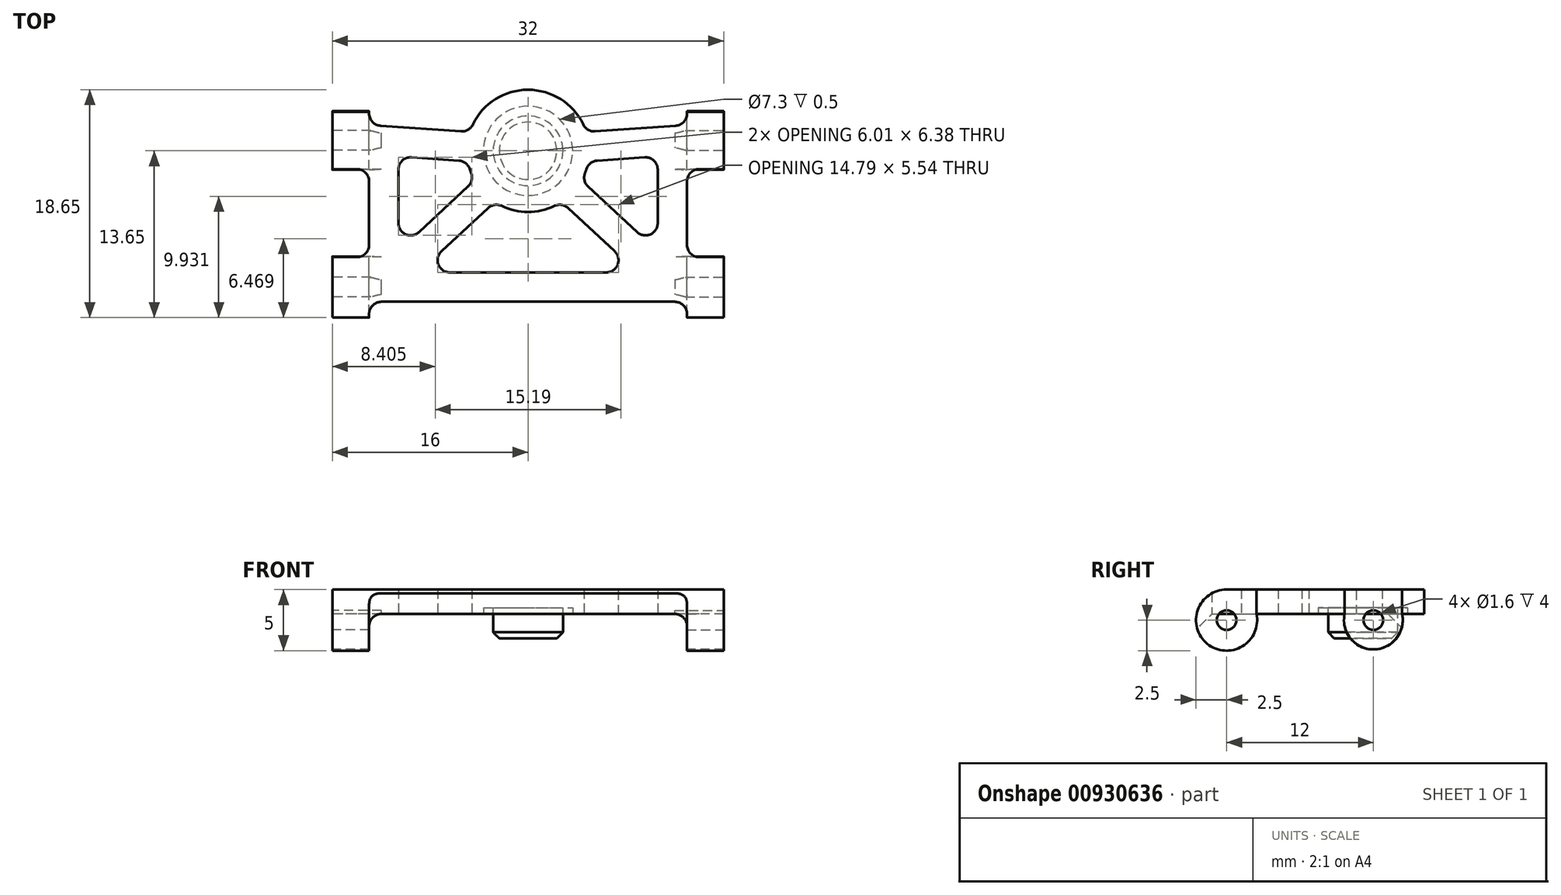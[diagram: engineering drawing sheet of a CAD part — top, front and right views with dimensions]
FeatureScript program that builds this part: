
annotation { "Feature Type Name" : "Feature", "Feature Type Description" : "" }
export const myFeature = defineFeature(function(context is Context, id is Id, definition is map)
    precondition{}
    {
        {
            var Q0;
            Q0=qCreatedBy(makeId("Right.planeOp"),FACE);
            var sketch = newSketch(context, id + "F0", { "sketchPlane" : qUnion([Q0])});
            skArc(sketch, "E0", {"start": v(0, 2.5) * mm, "mid": v(-1.58, -1.94) * mm, "end": v(2.45, 0.5) * mm});
            skArc(sketch, "E1", {"start": v(9.65, 0.5) * mm, "mid": v(12, -2.4) * mm, "end": v(14.35, 0.5) * mm});
            skLineSegment(sketch, "E2", {"start": v(2.45, 0.5) * mm, "end": v(9.65, 0.5) * mm});
            skLineSegment(sketch, "E3", {"start": v(16.35, 2.5) * mm, "end": v(16.35, 0.5) * mm});
            skLineSegment(sketch, "E4", {"start": v(16.35, 0.5) * mm, "end": v(14.35, 0.5) * mm});
            skLineSegment(sketch, "E5", {"start": v(16.35, 2.5) * mm, "end": v(0, 2.5) * mm});
            skSolve(sketch);
        }
        {
            var Q0;
            Q0=qSketchRegion(id+"F0",true);
            extrude(context, id + "F1", {"entities" : qUnion([Q0]), "depth" : 32 * mm, "offsetDistance" : 25 * mm});
        }
        {
            var Q0;
            Q0=makeQuery(id+"F1.opExtrude","SWEPT_FACE",FACE,{"disambiguationData":[OSD([sQuery(id+"F0.wireOp",EDGE,"E3")])]});
            var sketch = newSketch(context, id + "F2", { "sketchPlane" : qUnion([Q0])});
            skLineSegment(sketch, "E6.bottom", {"start": v(-29, 0.5) * mm, "end": v(-3, 0.5) * mm});
            skLineSegment(sketch, "E6.top", {"start": v(-29, -2.5) * mm, "end": v(-3, -2.5) * mm});
            skLineSegment(sketch, "E6.left", {"start": v(-29, 0.5) * mm, "end": v(-29, -2.5) * mm});
            skLineSegment(sketch, "E6.right", {"start": v(-3, 0.5) * mm, "end": v(-3, -2.5) * mm});
            skSolve(sketch);
        }
        {
            var Q0;
            Q0=qSketchRegion(id+"F2",true);
            extrude(context, id + "F3", {"entities" : qUnion([Q0]), "operationType" : NewBodyOperationType.REMOVE, "endBound" : BoundingType.THROUGH_ALL, "oppositeDirection" : true, "depth" : 25 * mm, "offsetDistance" : 25 * mm});
        }
        {
            var Q0;
            Q0=makeQuery(id+"F1.opExtrude","CAP_FACE",FACE,{"disambiguationData":[OSD([sQuery(id+"F0.wireOp",EDGE,"E0"),sQuery(id+"F0.wireOp",EDGE,"E1"),sQuery(id+"F0.wireOp",EDGE,"E2"),sQuery(id+"F0.wireOp",EDGE,"E3"),sQuery(id+"F0.wireOp",EDGE,"E4"),sQuery(id+"F0.wireOp",EDGE,"E5")])],"isStart":false});
            var sketch = newSketch(context, id + "F4", { "sketchPlane" : qUnion([Q0])});
            skCircle(sketch, "E7", {"center": v(0, 0) * mm, "radius": 0.8 * mm});
            skCircle(sketch, "E8", {"center": v(12, 0) * mm, "radius": 0.8 * mm});
            skSolve(sketch);
        }
        {
            var Q0;
            Q0=qSketchRegion(id+"F4",true);
            extrude(context, id + "F5", {"entities" : qUnion([Q0]), "operationType" : NewBodyOperationType.REMOVE, "oppositeDirection" : true, "depth" : 4 * mm, "offsetDistance" : 25 * mm});
        }
        {
            var Q0;
            Q0=makeQuery(id+"F1.opExtrude","CAP_FACE",FACE,{"disambiguationData":[OSD([sQuery(id+"F0.wireOp",EDGE,"E0"),sQuery(id+"F0.wireOp",EDGE,"E1"),sQuery(id+"F0.wireOp",EDGE,"E2"),sQuery(id+"F0.wireOp",EDGE,"E3"),sQuery(id+"F0.wireOp",EDGE,"E4"),sQuery(id+"F0.wireOp",EDGE,"E5")])],"isStart":true});
            var sketch = newSketch(context, id + "F6", { "sketchPlane" : qUnion([Q0])});
            skCircle(sketch, "E9", {"center": v(0, 0) * mm, "radius": 0.8 * mm});
            skCircle(sketch, "E10", {"center": v(-12, 0) * mm, "radius": 0.8 * mm});
            skSolve(sketch);
        }
        {
            var Q0;
            Q0=qSketchRegion(id+"F6",true);
            extrude(context, id + "F7", {"entities" : qUnion([Q0]), "operationType" : NewBodyOperationType.REMOVE, "oppositeDirection" : true, "depth" : 4 * mm, "offsetDistance" : 25 * mm});
        }
        {
            var Q0;
            Q0=makeQuery(id+"F3.boolean.opBoolean","MERGE",FACE,{"derivedFrom":[makeQuery(id+"F1.opExtrude","SWEPT_FACE",FACE,{"disambiguationData":[OSD([sQuery(id+"F0.wireOp",EDGE,"E2")])]}),makeQuery(id+"F1.opExtrude","SWEPT_FACE",FACE,{"disambiguationData":[OSD([sQuery(id+"F0.wireOp",EDGE,"E4")])]}),makeQuery(id+"F3.opExtrude","SWEPT_FACE",FACE,{"disambiguationData":[OSD([sQuery(id+"F2.wireOp",EDGE,"E6.bottom")])]})]});
            var sketch = newSketch(context, id + "F8", { "sketchPlane" : qUnion([Q0])});
            skLineSegment(sketch, "E11", {"start": v(16, 2.45) * mm, "end": v(16, -16.35) * mm, "construction": true});
            skCircle(sketch, "E12", {"center": v(16, -11.15) * mm, "radius": 2.85 * mm});
            skSolve(sketch);
        }
        {
            var Q0;
            Q0=qSketchRegion(id+"F8",true);
            extrude(context, id + "F9", {"entities" : qUnion([Q0]), "operationType" : NewBodyOperationType.ADD, "depth" : 2 * mm, "offsetDistance" : 25 * mm});
        }
        {
            var Q0;
            Q0=makeQuery(id+"F3.boolean.opBoolean","MERGE",FACE,{"derivedFrom":[makeQuery(id+"F1.opExtrude","SWEPT_FACE",FACE,{"disambiguationData":[OSD([sQuery(id+"F0.wireOp",EDGE,"E2")])]}),makeQuery(id+"F1.opExtrude","SWEPT_FACE",FACE,{"disambiguationData":[OSD([sQuery(id+"F0.wireOp",EDGE,"E4")])]}),makeQuery(id+"F3.opExtrude","SWEPT_FACE",FACE,{"disambiguationData":[OSD([sQuery(id+"F2.wireOp",EDGE,"E6.bottom")])]})]});
            var sketch = newSketch(context, id + "F10", { "sketchPlane" : qUnion([Q0])});
            skArc(sketch, "E13", {"start": v(18.74, -6.97) * mm, "mid": v(16, -6.15) * mm, "end": v(13.26, -6.97) * mm});
            skLineSegment(sketch, "E14.bottom", {"start": v(0, -2.45) * mm, "end": v(3, -2.45) * mm});
            skLineSegment(sketch, "E14.top", {"start": v(0, -9.65) * mm, "end": v(3, -9.65) * mm});
            skLineSegment(sketch, "E14.left", {"start": v(0, -2.45) * mm, "end": v(0, -9.65) * mm});
            skLineSegment(sketch, "E14.right", {"start": v(3, -2.45) * mm, "end": v(3, -9.65) * mm});
            skLineSegment(sketch, "E15.bottom", {"start": v(29, -2.45) * mm, "end": v(32, -2.45) * mm});
            skLineSegment(sketch, "E15.top", {"start": v(29, -9.65) * mm, "end": v(32, -9.65) * mm});
            skLineSegment(sketch, "E15.left", {"start": v(29, -2.45) * mm, "end": v(29, -9.65) * mm});
            skLineSegment(sketch, "E15.right", {"start": v(32, -2.45) * mm, "end": v(32, -9.65) * mm});
            skLineSegment(sketch, "E16.bottom", {"start": v(0, -14.35) * mm, "end": v(3, -14.35) * mm});
            skLineSegment(sketch, "E16.left", {"start": v(0, -14.35) * mm, "end": v(0, -16.35) * mm});
            skLineSegment(sketch, "E17.bottom", {"start": v(29, -14.35) * mm, "end": v(32, -14.35) * mm});
            skLineSegment(sketch, "E17.right", {"start": v(32, -14.35) * mm, "end": v(32, -16.35) * mm});
            skLineSegment(sketch, "E18", {"start": v(3, 1.2) * mm, "end": v(29, 1.2) * mm});
            skLineSegment(sketch, "E19", {"start": v(4, 0) * mm, "end": v(28, 0) * mm, "construction": true});
            skLineSegment(sketch, "E20", {"start": v(4, -12) * mm, "end": v(16, -11.15) * mm, "construction": true});
            skLineSegment(sketch, "E21", {"start": v(28, -12) * mm, "end": v(16, -11.15) * mm, "construction": true});
            skLineSegment(sketch, "E22", {"start": v(4, 0) * mm, "end": v(16, -11.15) * mm, "construction": true});
            skLineSegment(sketch, "E23", {"start": v(16, -11.15) * mm, "end": v(28, 0) * mm, "construction": true});
            skLineSegment(sketch, "E24", {"start": v(5.4, -10.7) * mm, "end": v(11.07, -10.3) * mm});
            skLineSegment(sketch, "E25", {"start": v(3, -13.27) * mm, "end": v(11.24, -12.69) * mm});
            skLineSegment(sketch, "E26", {"start": v(26.6, -10.7) * mm, "end": v(20.93, -10.3) * mm});
            skLineSegment(sketch, "E27", {"start": v(29, -13.27) * mm, "end": v(20.76, -12.69) * mm});
            skLineSegment(sketch, "E28", {"start": v(3, -13.27) * mm, "end": v(3, -14.35) * mm});
            skLineSegment(sketch, "E29", {"start": v(29, -13.27) * mm, "end": v(29, -14.35) * mm});
            skLineSegment(sketch, "E30", {"start": v(0, -16.35) * mm, "end": v(16, -16.35) * mm});
            skLineSegment(sketch, "E31", {"start": v(16, -16.35) * mm, "end": v(32, -16.35) * mm});
            skLineSegment(sketch, "E32", {"start": v(7.05, -1.2) * mm, "end": v(13.26, -6.97) * mm});
            skLineSegment(sketch, "E33", {"start": v(24.95, -1.2) * mm, "end": v(18.74, -6.97) * mm});
            skLineSegment(sketch, "E34", {"start": v(5.4, -2.94) * mm, "end": v(11.63, -8.73) * mm});
            skLineSegment(sketch, "E35", {"start": v(26.6, -2.94) * mm, "end": v(20.37, -8.73) * mm});
            skLineSegment(sketch, "E36", {"start": v(5.4, -2.94) * mm, "end": v(5.4, -10.7) * mm});
            skLineSegment(sketch, "E37", {"start": v(26.6, -2.94) * mm, "end": v(26.6, -10.7) * mm});
            skLineSegment(sketch, "E38.trimOffspring", {"start": v(7.05, -1.2) * mm, "end": v(24.95, -1.2) * mm});
            skLineSegment(sketch, "E39", {"start": v(3, 1.2) * mm, "end": v(3, 2.45) * mm});
            skLineSegment(sketch, "E40", {"start": v(3, 2.45) * mm, "end": v(29, 2.45) * mm});
            skLineSegment(sketch, "E41", {"start": v(29, 2.45) * mm, "end": v(29, 1.2) * mm});
            skArc(sketch, "E42.trimOffspring", {"start": v(11.63, -8.73) * mm, "mid": v(11.28, -9.49) * mm, "end": v(11.07, -10.3) * mm});
            skArc(sketch, "E43.trimOffspring", {"start": v(11.24, -12.69) * mm, "mid": v(16, -16.15) * mm, "end": v(20.76, -12.69) * mm});
            skArc(sketch, "E44.trimOffspring", {"start": v(20.93, -10.3) * mm, "mid": v(20.72, -9.49) * mm, "end": v(20.37, -8.73) * mm});
            skPoint(sketch, "E45", {"position": v(28, 0) * mm});
            skSolve(sketch);
        }
        {
            var Q0;
            Q0=qSketchRegion(id+"F10",true);
            extrude(context, id + "F11", {"entities" : qUnion([Q0]), "operationType" : NewBodyOperationType.REMOVE, "endBound" : BoundingType.UP_TO_NEXT, "oppositeDirection" : true, "depth" : 25 * mm, "offsetDistance" : 25 * mm});
        }
        {
            var Q0;
            Q0=makeQuery(id+"F11.boolean.opBoolean","COPY",EDGE,{"derivedFrom":makeQuery(id+"F11.opExtrude","SWEPT_EDGE",EDGE,{"disambiguationData":[OSD([sQuery(id+"F0.wireOp",EDGE,"E1"),sQuery(id+"F0.wireOp",EDGE,"E3"),sQuery(id+"F0.wireOp",EDGE,"E4"),sQuery(id+"F2.wireOp",EDGE,"E6.bottom"),sQuery(id+"F2.wireOp",EDGE,"E6.left"),sQuery(id+"F10.wireOp",EDGE,"E15.top"),sQuery(id+"F10.wireOp",EDGE,"E15.left")])]})});
            var Q1;
            Q1=makeQuery(id+"F11.boolean.opBoolean","COPY",EDGE,{"derivedFrom":makeQuery(id+"F11.opExtrude","SWEPT_EDGE",EDGE,{"disambiguationData":[OSD([sQuery(id+"F0.wireOp",EDGE,"E0"),sQuery(id+"F0.wireOp",EDGE,"E3"),sQuery(id+"F0.wireOp",EDGE,"E4"),sQuery(id+"F2.wireOp",EDGE,"E6.bottom"),sQuery(id+"F2.wireOp",EDGE,"E6.left"),sQuery(id+"F10.wireOp",EDGE,"E15.bottom"),sQuery(id+"F10.wireOp",EDGE,"E15.left")])]})});
            var Q2;
            Q2=makeQuery(id+"F11.boolean.opBoolean","COPY",EDGE,{"derivedFrom":makeQuery(id+"F11.opExtrude","SWEPT_EDGE",EDGE,{"disambiguationData":[OSD([sQuery(id+"F0.wireOp",EDGE,"E0"),sQuery(id+"F0.wireOp",EDGE,"E3"),sQuery(id+"F0.wireOp",EDGE,"E4"),sQuery(id+"F2.wireOp",EDGE,"E6.bottom"),sQuery(id+"F2.wireOp",EDGE,"E6.right"),sQuery(id+"F10.wireOp",EDGE,"E14.bottom"),sQuery(id+"F10.wireOp",EDGE,"E14.right")])]})});
            var Q3;
            Q3=makeQuery(id+"F11.boolean.opBoolean","COPY",EDGE,{"derivedFrom":makeQuery(id+"F11.opExtrude","SWEPT_EDGE",EDGE,{"disambiguationData":[OSD([sQuery(id+"F0.wireOp",EDGE,"E1"),sQuery(id+"F0.wireOp",EDGE,"E3"),sQuery(id+"F0.wireOp",EDGE,"E4"),sQuery(id+"F2.wireOp",EDGE,"E6.bottom"),sQuery(id+"F2.wireOp",EDGE,"E6.right"),sQuery(id+"F10.wireOp",EDGE,"E14.top"),sQuery(id+"F10.wireOp",EDGE,"E14.right")])]})});
            var Q4;
            Q4=makeQuery(id+"F11.boolean.opBoolean","COPY",EDGE,{"derivedFrom":makeQuery(id+"F11.opExtrude","SWEPT_EDGE",EDGE,{"disambiguationData":[OSD([sQuery(id+"F0.wireOp",EDGE,"E3"),sQuery(id+"F0.wireOp",EDGE,"E4"),sQuery(id+"F2.wireOp",EDGE,"E6.bottom"),sQuery(id+"F2.wireOp",EDGE,"E6.left"),sQuery(id+"F10.wireOp",EDGE,"E18"),sQuery(id+"F10.wireOp",EDGE,"E41")])]})});
            var Q5;
            Q5=makeQuery(id+"F11.boolean.opBoolean","COPY",EDGE,{"derivedFrom":makeQuery(id+"F11.opExtrude","SWEPT_EDGE",EDGE,{"disambiguationData":[OSD([sQuery(id+"F0.wireOp",EDGE,"E3"),sQuery(id+"F0.wireOp",EDGE,"E4"),sQuery(id+"F2.wireOp",EDGE,"E6.bottom"),sQuery(id+"F2.wireOp",EDGE,"E6.right"),sQuery(id+"F10.wireOp",EDGE,"E18"),sQuery(id+"F10.wireOp",EDGE,"E39")])]})});
            var Q6;
            Q6=makeQuery(id+"F11.boolean.opBoolean","COPY",EDGE,{"derivedFrom":makeQuery(id+"F11.opExtrude","SWEPT_EDGE",EDGE,{"disambiguationData":[OSD([sQuery(id+"F0.wireOp",EDGE,"E3"),sQuery(id+"F0.wireOp",EDGE,"E4"),sQuery(id+"F2.wireOp",EDGE,"E6.bottom"),sQuery(id+"F2.wireOp",EDGE,"E6.right"),sQuery(id+"F10.wireOp",EDGE,"E25"),sQuery(id+"F10.wireOp",EDGE,"E28")])]})});
            var Q7;
            Q7=makeQuery(id+"F11.boolean.opBoolean","COPY",EDGE,{"derivedFrom":makeQuery(id+"F11.opExtrude","SWEPT_EDGE",EDGE,{"disambiguationData":[OSD([sQuery(id+"F0.wireOp",EDGE,"E3"),sQuery(id+"F0.wireOp",EDGE,"E4"),sQuery(id+"F2.wireOp",EDGE,"E6.bottom"),sQuery(id+"F2.wireOp",EDGE,"E6.left"),sQuery(id+"F10.wireOp",EDGE,"E27"),sQuery(id+"F10.wireOp",EDGE,"E29")])]})});
            fillet(context, id + "F12", {"entities" : qUnion([Q0, Q1, Q2, Q3, Q4, Q5, Q6, Q7]), "radius" : 1 * mm, "tangentPropagation" : true, "allowEdgeOverflow" : false});
        }
        {
            var Q0;
            {var subQ0=makeQuery(id+"F1.opExtrude","SWEPT_FACE",FACE,{"disambiguationData":[OSD([sQuery(id+"F0.wireOp",EDGE,"E2")])]});var subQ1=sQuery(id+"F0.wireOp",EDGE,"E4");var subQ2=makeQuery(id+"F1.opExtrude","SWEPT_FACE",FACE,{"disambiguationData":[OSD([subQ1])]});var subQ3=sQuery(id+"F2.wireOp",EDGE,"E6.bottom");var subQ4=makeQuery(id+"F3.opExtrude","SWEPT_FACE",FACE,{"disambiguationData":[OSD([subQ3])]});var subQ5=makeQuery(id+"F1.opExtrude","SWEPT_FACE",FACE,{"disambiguationData":[OSD([sQuery(id+"F0.wireOp",EDGE,"E0")])]});var subQ6=sQuery(id+"F2.wireOp",EDGE,"E6.left");var subQ7=makeQuery(id+"F3.opExtrude","SWEPT_FACE",FACE,{"disambiguationData":[OSD([subQ6])]});Q0=makeQuery(id+"F5.boolean.opBoolean","SPLIT",EDGE,{"disambiguationData":[topologyDisambiguationEdgeConnected([subQ0,subQ2,subQ4,makeQuery(id+"F3.boolean.opBoolean","COPY",FACE,{"disambiguationData":[TD([subQ5])],"derivedFrom":subQ7})]),OD(0.0)],"derivedFrom":makeQuery(id+"F3.boolean.opBoolean","COPY",EDGE,{"disambiguationData":[TD([subQ5])],"derivedFrom":makeQuery(id+"F3.opExtrude","SWEPT_EDGE",EDGE,{"disambiguationData":[OSD([sQuery(id+"F0.wireOp",EDGE,"E3"),subQ1,subQ3,subQ6])]})})});}
            var Q1;
            {var subQ0=makeQuery(id+"F1.opExtrude","SWEPT_FACE",FACE,{"disambiguationData":[OSD([sQuery(id+"F0.wireOp",EDGE,"E2")])]});var subQ1=sQuery(id+"F0.wireOp",EDGE,"E4");var subQ2=makeQuery(id+"F1.opExtrude","SWEPT_FACE",FACE,{"disambiguationData":[OSD([subQ1])]});var subQ3=sQuery(id+"F2.wireOp",EDGE,"E6.bottom");var subQ4=makeQuery(id+"F3.opExtrude","SWEPT_FACE",FACE,{"disambiguationData":[OSD([subQ3])]});var subQ5=makeQuery(id+"F1.opExtrude","SWEPT_FACE",FACE,{"disambiguationData":[OSD([sQuery(id+"F0.wireOp",EDGE,"E0")])]});var subQ6=sQuery(id+"F2.wireOp",EDGE,"E6.left");var subQ7=makeQuery(id+"F3.opExtrude","SWEPT_FACE",FACE,{"disambiguationData":[OSD([subQ6])]});Q1=makeQuery(id+"F5.boolean.opBoolean","SPLIT",EDGE,{"disambiguationData":[topologyDisambiguationEdgeConnected([subQ0,subQ2,subQ4,makeQuery(id+"F3.boolean.opBoolean","COPY",FACE,{"disambiguationData":[TD([subQ5])],"derivedFrom":subQ7})]),OD(1.0)],"derivedFrom":makeQuery(id+"F3.boolean.opBoolean","COPY",EDGE,{"disambiguationData":[TD([subQ5])],"derivedFrom":makeQuery(id+"F3.opExtrude","SWEPT_EDGE",EDGE,{"disambiguationData":[OSD([sQuery(id+"F0.wireOp",EDGE,"E3"),subQ1,subQ3,subQ6])]})})});}
            var Q2;
            {var subQ0=makeQuery(id+"F1.opExtrude","SWEPT_FACE",FACE,{"disambiguationData":[OSD([sQuery(id+"F0.wireOp",EDGE,"E2")])]});var subQ1=sQuery(id+"F0.wireOp",EDGE,"E4");var subQ2=makeQuery(id+"F1.opExtrude","SWEPT_FACE",FACE,{"disambiguationData":[OSD([subQ1])]});var subQ3=sQuery(id+"F2.wireOp",EDGE,"E6.bottom");var subQ4=makeQuery(id+"F3.opExtrude","SWEPT_FACE",FACE,{"disambiguationData":[OSD([subQ3])]});var subQ5=makeQuery(id+"F1.opExtrude","SWEPT_FACE",FACE,{"disambiguationData":[OSD([sQuery(id+"F0.wireOp",EDGE,"E0")])]});var subQ6=sQuery(id+"F2.wireOp",EDGE,"E6.right");var subQ7=makeQuery(id+"F3.opExtrude","SWEPT_FACE",FACE,{"disambiguationData":[OSD([subQ6])]});Q2=makeQuery(id+"F7.boolean.opBoolean","SPLIT",EDGE,{"disambiguationData":[topologyDisambiguationEdgeConnected([subQ0,subQ2,subQ4,makeQuery(id+"F3.boolean.opBoolean","COPY",FACE,{"disambiguationData":[TD([subQ5])],"derivedFrom":subQ7})]),OD(1.0)],"derivedFrom":makeQuery(id+"F3.boolean.opBoolean","COPY",EDGE,{"disambiguationData":[TD([subQ5])],"derivedFrom":makeQuery(id+"F3.opExtrude","SWEPT_EDGE",EDGE,{"disambiguationData":[OSD([sQuery(id+"F0.wireOp",EDGE,"E3"),subQ1,subQ3,subQ6])]})})});}
            var Q3;
            {var subQ0=makeQuery(id+"F1.opExtrude","SWEPT_FACE",FACE,{"disambiguationData":[OSD([sQuery(id+"F0.wireOp",EDGE,"E2")])]});var subQ1=sQuery(id+"F0.wireOp",EDGE,"E4");var subQ2=makeQuery(id+"F1.opExtrude","SWEPT_FACE",FACE,{"disambiguationData":[OSD([subQ1])]});var subQ3=sQuery(id+"F2.wireOp",EDGE,"E6.bottom");var subQ4=makeQuery(id+"F3.opExtrude","SWEPT_FACE",FACE,{"disambiguationData":[OSD([subQ3])]});var subQ5=makeQuery(id+"F1.opExtrude","SWEPT_FACE",FACE,{"disambiguationData":[OSD([sQuery(id+"F0.wireOp",EDGE,"E0")])]});var subQ6=sQuery(id+"F2.wireOp",EDGE,"E6.right");var subQ7=makeQuery(id+"F3.opExtrude","SWEPT_FACE",FACE,{"disambiguationData":[OSD([subQ6])]});Q3=makeQuery(id+"F7.boolean.opBoolean","SPLIT",EDGE,{"disambiguationData":[topologyDisambiguationEdgeConnected([subQ0,subQ2,subQ4,makeQuery(id+"F3.boolean.opBoolean","COPY",FACE,{"disambiguationData":[TD([subQ5])],"derivedFrom":subQ7})]),OD(0.0)],"derivedFrom":makeQuery(id+"F3.boolean.opBoolean","COPY",EDGE,{"disambiguationData":[TD([subQ5])],"derivedFrom":makeQuery(id+"F3.opExtrude","SWEPT_EDGE",EDGE,{"disambiguationData":[OSD([sQuery(id+"F0.wireOp",EDGE,"E3"),subQ1,subQ3,subQ6])]})})});}
            var Q4;
            {var subQ0=makeQuery(id+"F1.opExtrude","SWEPT_FACE",FACE,{"disambiguationData":[OSD([sQuery(id+"F0.wireOp",EDGE,"E2")])]});var subQ1=sQuery(id+"F0.wireOp",EDGE,"E4");var subQ2=makeQuery(id+"F1.opExtrude","SWEPT_FACE",FACE,{"disambiguationData":[OSD([subQ1])]});var subQ3=makeQuery(id+"F1.opExtrude","SWEPT_FACE",FACE,{"disambiguationData":[OSD([sQuery(id+"F0.wireOp",EDGE,"E1")])]});var subQ4=sQuery(id+"F2.wireOp",EDGE,"E6.bottom");var subQ5=makeQuery(id+"F3.opExtrude","SWEPT_FACE",FACE,{"disambiguationData":[OSD([subQ4])]});var subQ6=sQuery(id+"F2.wireOp",EDGE,"E6.right");var subQ7=makeQuery(id+"F3.opExtrude","SWEPT_FACE",FACE,{"disambiguationData":[OSD([subQ6])]});Q4=makeQuery(id+"F7.boolean.opBoolean","SPLIT",EDGE,{"disambiguationData":[topologyDisambiguationEdgeConnected([subQ0,subQ2,subQ5,makeQuery(id+"F3.boolean.opBoolean","COPY",FACE,{"disambiguationData":[TD([subQ3])],"derivedFrom":subQ7})]),OD(0.0)],"derivedFrom":makeQuery(id+"F3.boolean.opBoolean","COPY",EDGE,{"disambiguationData":[TD([subQ3])],"derivedFrom":makeQuery(id+"F3.opExtrude","SWEPT_EDGE",EDGE,{"disambiguationData":[OSD([sQuery(id+"F0.wireOp",EDGE,"E3"),subQ1,subQ4,subQ6])]})})});}
            var Q5;
            {var subQ0=makeQuery(id+"F1.opExtrude","SWEPT_FACE",FACE,{"disambiguationData":[OSD([sQuery(id+"F0.wireOp",EDGE,"E2")])]});var subQ1=sQuery(id+"F0.wireOp",EDGE,"E4");var subQ2=makeQuery(id+"F1.opExtrude","SWEPT_FACE",FACE,{"disambiguationData":[OSD([subQ1])]});var subQ3=makeQuery(id+"F1.opExtrude","SWEPT_FACE",FACE,{"disambiguationData":[OSD([sQuery(id+"F0.wireOp",EDGE,"E1")])]});var subQ4=sQuery(id+"F2.wireOp",EDGE,"E6.bottom");var subQ5=makeQuery(id+"F3.opExtrude","SWEPT_FACE",FACE,{"disambiguationData":[OSD([subQ4])]});var subQ6=sQuery(id+"F2.wireOp",EDGE,"E6.right");var subQ7=makeQuery(id+"F3.opExtrude","SWEPT_FACE",FACE,{"disambiguationData":[OSD([subQ6])]});Q5=makeQuery(id+"F7.boolean.opBoolean","SPLIT",EDGE,{"disambiguationData":[topologyDisambiguationEdgeConnected([subQ0,subQ2,subQ5,makeQuery(id+"F3.boolean.opBoolean","COPY",FACE,{"disambiguationData":[TD([subQ3])],"derivedFrom":subQ7})]),OD(1.0)],"derivedFrom":makeQuery(id+"F3.boolean.opBoolean","COPY",EDGE,{"disambiguationData":[TD([subQ3])],"derivedFrom":makeQuery(id+"F3.opExtrude","SWEPT_EDGE",EDGE,{"disambiguationData":[OSD([sQuery(id+"F0.wireOp",EDGE,"E3"),subQ1,subQ4,subQ6])]})})});}
            var Q6;
            {var subQ0=makeQuery(id+"F1.opExtrude","SWEPT_FACE",FACE,{"disambiguationData":[OSD([sQuery(id+"F0.wireOp",EDGE,"E2")])]});var subQ1=makeQuery(id+"F1.opExtrude","SWEPT_FACE",FACE,{"disambiguationData":[OSD([sQuery(id+"F0.wireOp",EDGE,"E1")])]});var subQ2=sQuery(id+"F2.wireOp",EDGE,"E6.bottom");var subQ3=makeQuery(id+"F3.opExtrude","SWEPT_FACE",FACE,{"disambiguationData":[OSD([subQ2])]});var subQ4=sQuery(id+"F0.wireOp",EDGE,"E4");var subQ5=makeQuery(id+"F1.opExtrude","SWEPT_FACE",FACE,{"disambiguationData":[OSD([subQ4])]});var subQ6=sQuery(id+"F2.wireOp",EDGE,"E6.left");var subQ7=makeQuery(id+"F3.opExtrude","SWEPT_FACE",FACE,{"disambiguationData":[OSD([subQ6])]});Q6=makeQuery(id+"F5.boolean.opBoolean","SPLIT",EDGE,{"disambiguationData":[topologyDisambiguationEdgeConnected([subQ0,subQ5,subQ3,makeQuery(id+"F3.boolean.opBoolean","COPY",FACE,{"disambiguationData":[TD([subQ1])],"derivedFrom":subQ7})]),OD(0.0)],"derivedFrom":makeQuery(id+"F3.boolean.opBoolean","COPY",EDGE,{"disambiguationData":[TD([subQ1])],"derivedFrom":makeQuery(id+"F3.opExtrude","SWEPT_EDGE",EDGE,{"disambiguationData":[OSD([sQuery(id+"F0.wireOp",EDGE,"E3"),subQ4,subQ2,subQ6])]})})});}
            var Q7;
            {var subQ0=makeQuery(id+"F1.opExtrude","SWEPT_FACE",FACE,{"disambiguationData":[OSD([sQuery(id+"F0.wireOp",EDGE,"E2")])]});var subQ1=makeQuery(id+"F1.opExtrude","SWEPT_FACE",FACE,{"disambiguationData":[OSD([sQuery(id+"F0.wireOp",EDGE,"E1")])]});var subQ2=sQuery(id+"F2.wireOp",EDGE,"E6.bottom");var subQ3=makeQuery(id+"F3.opExtrude","SWEPT_FACE",FACE,{"disambiguationData":[OSD([subQ2])]});var subQ4=sQuery(id+"F0.wireOp",EDGE,"E4");var subQ5=makeQuery(id+"F1.opExtrude","SWEPT_FACE",FACE,{"disambiguationData":[OSD([subQ4])]});var subQ6=sQuery(id+"F2.wireOp",EDGE,"E6.left");var subQ7=makeQuery(id+"F3.opExtrude","SWEPT_FACE",FACE,{"disambiguationData":[OSD([subQ6])]});Q7=makeQuery(id+"F5.boolean.opBoolean","SPLIT",EDGE,{"disambiguationData":[topologyDisambiguationEdgeConnected([subQ0,subQ5,subQ3,makeQuery(id+"F3.boolean.opBoolean","COPY",FACE,{"disambiguationData":[TD([subQ1])],"derivedFrom":subQ7})]),OD(1.0)],"derivedFrom":makeQuery(id+"F3.boolean.opBoolean","COPY",EDGE,{"disambiguationData":[TD([subQ1])],"derivedFrom":makeQuery(id+"F3.opExtrude","SWEPT_EDGE",EDGE,{"disambiguationData":[OSD([sQuery(id+"F0.wireOp",EDGE,"E3"),subQ4,subQ2,subQ6])]})})});}
            fillet(context, id + "F13", {"entities" : qUnion([Q0, Q1, Q2, Q3, Q4, Q5, Q6, Q7]), "radius" : 1 * mm, "tangentPropagation" : true, "allowEdgeOverflow" : false});
        }
        {
            var Q0;
            Q0=makeQuery(id+"F3.boolean.opBoolean","MERGE",FACE,{"derivedFrom":[makeQuery(id+"F1.opExtrude","SWEPT_FACE",FACE,{"disambiguationData":[OSD([sQuery(id+"F0.wireOp",EDGE,"E2")])]}),makeQuery(id+"F1.opExtrude","SWEPT_FACE",FACE,{"disambiguationData":[OSD([sQuery(id+"F0.wireOp",EDGE,"E4")])]}),makeQuery(id+"F3.opExtrude","SWEPT_FACE",FACE,{"disambiguationData":[OSD([sQuery(id+"F2.wireOp",EDGE,"E6.bottom")])]})]});
            var sketch = newSketch(context, id + "F14", { "sketchPlane" : qUnion([Q0])});
            skCircle(sketch, "E46", {"center": v(16, -11.15) * mm, "radius": 3.65 * mm});
            skCircle(sketch, "E47", {"center": v(16, -11.15) * mm, "radius": 2.85 * mm});
            skSolve(sketch);
        }
        {
            var Q0;
            Q0=qSketchRegion(id+"F14",true);
            extrude(context, id + "F15", {"entities" : qUnion([Q0]), "operationType" : NewBodyOperationType.REMOVE, "oppositeDirection" : true, "depth" : 0.5 * mm, "offsetDistance" : 25 * mm});
        }
        {
            var Q0;
            Q0=makeQuery(id+"F11.boolean.opBoolean","COPY",EDGE,{"derivedFrom":makeQuery(id+"F11.opExtrude","SWEPT_EDGE",EDGE,{"disambiguationData":[OSD([sQuery(id+"F10.wireOp",EDGE,"E25"),sQuery(id+"F10.wireOp",EDGE,"E43.trimOffspring")])]})});
            var Q1;
            Q1=makeQuery(id+"F11.boolean.opBoolean","COPY",EDGE,{"derivedFrom":makeQuery(id+"F11.opExtrude","SWEPT_EDGE",EDGE,{"disambiguationData":[OSD([sQuery(id+"F10.wireOp",EDGE,"E27"),sQuery(id+"F10.wireOp",EDGE,"E43.trimOffspring")])]})});
            var Q2;
            Q2=makeQuery(id+"F11.boolean.opBoolean","COPY",EDGE,{"derivedFrom":makeQuery(id+"F11.opExtrude","SWEPT_EDGE",EDGE,{"disambiguationData":[OSD([sQuery(id+"F10.wireOp",EDGE,"E26"),sQuery(id+"F10.wireOp",EDGE,"E37")])]})});
            var Q3;
            Q3=makeQuery(id+"F11.boolean.opBoolean","COPY",EDGE,{"derivedFrom":makeQuery(id+"F11.opExtrude","SWEPT_EDGE",EDGE,{"disambiguationData":[OSD([sQuery(id+"F10.wireOp",EDGE,"E35"),sQuery(id+"F10.wireOp",EDGE,"E37")])]})});
            var Q4;
            Q4=makeQuery(id+"F11.boolean.opBoolean","COPY",EDGE,{"derivedFrom":makeQuery(id+"F11.opExtrude","SWEPT_EDGE",EDGE,{"disambiguationData":[OSD([sQuery(id+"F10.wireOp",EDGE,"E33"),sQuery(id+"F10.wireOp",EDGE,"E38.trimOffspring")])]})});
            var Q5;
            Q5=makeQuery(id+"F11.boolean.opBoolean","COPY",EDGE,{"derivedFrom":makeQuery(id+"F11.opExtrude","SWEPT_EDGE",EDGE,{"disambiguationData":[OSD([sQuery(id+"F10.wireOp",EDGE,"E13"),sQuery(id+"F10.wireOp",EDGE,"E33")])]})});
            var Q6;
            Q6=makeQuery(id+"F11.boolean.opBoolean","COPY",EDGE,{"derivedFrom":makeQuery(id+"F11.opExtrude","SWEPT_EDGE",EDGE,{"disambiguationData":[OSD([sQuery(id+"F10.wireOp",EDGE,"E35"),sQuery(id+"F10.wireOp",EDGE,"E44.trimOffspring")])]})});
            var Q7;
            Q7=makeQuery(id+"F11.boolean.opBoolean","COPY",EDGE,{"derivedFrom":makeQuery(id+"F11.opExtrude","SWEPT_EDGE",EDGE,{"disambiguationData":[OSD([sQuery(id+"F10.wireOp",EDGE,"E26"),sQuery(id+"F10.wireOp",EDGE,"E44.trimOffspring")])]})});
            var Q8;
            Q8=makeQuery(id+"F11.boolean.opBoolean","COPY",EDGE,{"derivedFrom":makeQuery(id+"F11.opExtrude","SWEPT_EDGE",EDGE,{"disambiguationData":[OSD([sQuery(id+"F10.wireOp",EDGE,"E32"),sQuery(id+"F10.wireOp",EDGE,"E38.trimOffspring")])]})});
            var Q9;
            Q9=makeQuery(id+"F11.boolean.opBoolean","COPY",EDGE,{"derivedFrom":makeQuery(id+"F11.opExtrude","SWEPT_EDGE",EDGE,{"disambiguationData":[OSD([sQuery(id+"F10.wireOp",EDGE,"E13"),sQuery(id+"F10.wireOp",EDGE,"E32")])]})});
            var Q10;
            Q10=makeQuery(id+"F11.boolean.opBoolean","COPY",EDGE,{"derivedFrom":makeQuery(id+"F11.opExtrude","SWEPT_EDGE",EDGE,{"disambiguationData":[OSD([sQuery(id+"F10.wireOp",EDGE,"E34"),sQuery(id+"F10.wireOp",EDGE,"E36")])]})});
            var Q11;
            Q11=makeQuery(id+"F11.boolean.opBoolean","COPY",EDGE,{"derivedFrom":makeQuery(id+"F11.opExtrude","SWEPT_EDGE",EDGE,{"disambiguationData":[OSD([sQuery(id+"F10.wireOp",EDGE,"E34"),sQuery(id+"F10.wireOp",EDGE,"E42.trimOffspring")])]})});
            var Q12;
            Q12=makeQuery(id+"F11.boolean.opBoolean","COPY",EDGE,{"derivedFrom":makeQuery(id+"F11.opExtrude","SWEPT_EDGE",EDGE,{"disambiguationData":[OSD([sQuery(id+"F10.wireOp",EDGE,"E24"),sQuery(id+"F10.wireOp",EDGE,"E42.trimOffspring")])]})});
            var Q13;
            Q13=makeQuery(id+"F11.boolean.opBoolean","COPY",EDGE,{"derivedFrom":makeQuery(id+"F11.opExtrude","SWEPT_EDGE",EDGE,{"disambiguationData":[OSD([sQuery(id+"F10.wireOp",EDGE,"E24"),sQuery(id+"F10.wireOp",EDGE,"E36")])]})});
            fillet(context, id + "F16", {"entities" : qUnion([Q0, Q1, Q2, Q3, Q4, Q5, Q6, Q7, Q8, Q9, Q10, Q11, Q12, Q13]), "radius" : 1 * mm, "tangentPropagation" : true, "allowEdgeOverflow" : false});
        }
        {
            var Q0;
            Q0=makeQuery(id+"F9.opExtrude","CAP_EDGE",EDGE,{"disambiguationData":[OSD([sQuery(id+"F8.wireOp",EDGE,"E12")])],"isStart":false});
            chamfer(context, id + "F17", {"entities" : qUnion([Q0]), "width" : 0.5 * mm, "tangentPropagation" : true});
        }
    });
